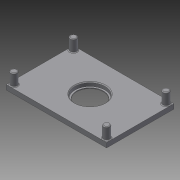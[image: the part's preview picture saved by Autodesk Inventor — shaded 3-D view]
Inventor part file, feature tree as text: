
AUTODESK INVENTOR PART (.ipt)
format: ipt  version: 2013 (Build 170138000, 138)  size: 138,240 bytes
history: native  units: mm
features: extrude x4, sketch x4, chamfer x1, fillet x1
ambient origin geometry x8: Origin, YZ Plane, XZ Plane, XY Plane, X Axis, Y Axis, Z Axis, Center Point
bodies: Solid1 (feature_tree)
feature tree (10):
  extrude  "Extrusion1"  Depth=127.7mm
  extrude  "Extrusion2"  Depth=38.0mm
  extrude  "Extrusion3"  Depth=34.0mm
  chamfer  "Chamfer1"  [1 undecoded]
  extrude  "Extrusion4"  Depth=5.0mm
  fillet  "Fillet1"  Radius=8.0mm
  sketch  "Sketch1"  dims[d0=85.5mm d2=127.7mm]
  sketch  "Sketch2"  dims[d3=6.0mm d4=0.0mm d5=38.0mm]
  sketch  "Sketch3"  dims[d7=5.0mm d8=0.0mm d9=34.0mm d11=0.0mm d12=0.0mm]
  sketch  "Sketch4"  dims[d13=1.0mm d14=2.0mm d15=45.0deg d16=5.0mm d18=8.0mm d19=15.0mm d20=0.0mm d21=1.0mm]
note: 1 required parameter value undecoded (feature->parameter linkage not recoverable at this tier; creation-order binding heuristic only, values carry confidence <= 0.55)
